FCSTD DOCUMENT  (FreeCAD 1.1R38827 (Git))
Label: composit_stand3_tech_sector_assembly
License: All rights reserved
LicenseURL: http://en.wikipedia.org/wiki/All_rights_reserved
objects: App::Link×5, App::DocumentObjectGroup×3, PartDesign::CoordinateSystem×1, App::FeaturePython×1, App::Part×1
note: 1 computed .brp shape members not serialized (recipe doc carries the construction recipe); baked Part::Feature solids carry a one-line shape summary decoded from their .brp
EXTERNAL_REF file=composit_stand3_tech_sector_hor_model.FCStd obj=Local_CS
EXTERNAL_REF file=composit_stand3_tech_sector_hor_model.FCStd obj=Body
EXTERNAL_REF file=composit_stand3_tech_sector_hor_model.FCStd obj=Local_CS001
EXTERNAL_REF file=composit_stand3_tech_sector_pillar_model.FCStd obj=Local_CS
EXTERNAL_REF file=composit_stand3_tech_sector_pillar_model.FCStd obj=Body
EXTERNAL_REF file=composit_stand3_tech_sector_plexiglass_model.FCStd obj=Local_CS
EXTERNAL_REF file=composit_stand3_tech_sector_plexiglass_model.FCStd obj=Body
EXTERNAL_REF file=composit_stand3_tech_sector_pillar_model.FCStd obj=Local_CS001
EXTERNAL_REF file=composit_stand3_tech_sector_pillar_model.FCStd obj=Body002

FEATURE [App::DocumentObjectGroup] Parts
FEATURE [PartDesign::CoordinateSystem] LCS_Origin
  AttacherType = Attacher::AttachEngine3D
  AttachmentSupport = -> [X_Axis]
  MapMode = 2
FEATURE [App::DocumentObjectGroup] Constraints
FEATURE [App::FeaturePython] Variables  # WARN: FeaturePython — macro-defined, semantics opaque (R4)
  Type = App::PropertyContainer
FEATURE [App::DocumentObjectGroup] Configurations
FEATURE [App::Link] hor
  AttachedBy = #Local_CS
  AttachedTo = Parent Assembly#LCS_Origin
  LinkedObject = -> <external composit_stand3_tech_sector_hor_model.FCStd>#Body
  SolverId = Asm4EE
  expr: Placement = LCS_Origin.Placement * AttachmentOffset * composit_stand3_tech_sector_hor_model#Local_CS.Placement ^ -1
FEATURE [App::Link] pillar
  AttachedBy = #Local_CS
  AttachedTo = hor#Local_CS001
  LinkPlacement = pos=(152.864,235.416,3) rot=(0,0,-1;0.523599rad)
  LinkedObject = -> <external composit_stand3_tech_sector_pillar_model.FCStd>#Body
  Placement = pos=(152.864,235.416,3) rot=(0,0,-1;0.523599rad)
  SolverId = Asm4EE
  expr: Placement = hor.Placement * composit_stand3_tech_sector_hor_model#Local_CS001.Placement * AttachmentOffset * composit_stand3_tech_sector_pillar_model#Local_CS.Placement ^ -1
FEATURE [App::Link] plexiglass
  AttachedBy = #Local_CS
  AttachedTo = Parent Assembly#LCS_Origin
  LinkedObject = -> <external composit_stand3_tech_sector_plexiglass_model.FCStd>#Body
  SolverId = Asm4EE
  expr: Placement = LCS_Origin.Placement * AttachmentOffset * composit_stand3_tech_sector_plexiglass_model#Local_CS.Placement ^ -1
FEATURE [App::Link] hor001
  AttachedBy = #Local_CS
  AttachedTo = Parent Assembly#LCS_Origin
  AttachmentOffset = pos=(0,0,419) rot=(1,0,0;3.14159rad)
  LinkPlacement = pos=(0,0,419) rot=(1,0,0;3.14159rad)
  LinkedObject = -> <external composit_stand3_tech_sector_hor_model.FCStd>#Body
  Placement = pos=(0,0,419) rot=(1,0,0;3.14159rad)
  SolverId = Asm4EE
  expr: Placement = LCS_Origin.Placement * AttachmentOffset * composit_stand3_tech_sector_hor_model#Local_CS.Placement ^ -1
FEATURE [App::Link] pillar_mirror
  AttachedBy = #Local_CS001
  AttachedTo = hor001#Local_CS001
  LinkPlacement = pos=(152.864,-235.416,3) rot=(0.965926,0.258819,0;3.14159rad)
  LinkedObject = -> <external composit_stand3_tech_sector_pillar_model.FCStd>#Body002
  Placement = pos=(152.864,-235.416,3) rot=(0.965926,0.258819,0;3.14159rad)
  SolverId = Asm4EE
  expr: Placement = hor001.Placement * composit_stand3_tech_sector_hor_model#Local_CS001.Placement * AttachmentOffset * composit_stand3_tech_sector_pillar_model#Local_CS001.Placement ^ -1
FEATURE [App::Part] Assembly
  AssemblyType = Part::Link
  Group = -> [LCS_Origin,Constraints,Variables,Configurations,hor,pillar,plexiglass,hor001,pillar_mirror]
  Origin = -> Origin
  Type = Assembly

RESOLVED EXTERNAL PARTS (link-assembly join: the EXTERNAL_REF files above that resolve inside this repo's crawl, each included once):
---- part composit_stand3_tech_sector_hor_model.FCStd = doc fcstd_c595c57b1264 ----
FCSTD DOCUMENT  (FreeCAD 1.1R38827 (Git))
Label: composit_stand3_tech_sector_hor_model
License: All rights reserved
LicenseURL: http://en.wikipedia.org/wiki/All_rights_reserved
objects: Part::FeaturePython×5, App::Link×3, PartDesign::SubShapeBinder×2, PartDesign::Body×2, PartDesign::CoordinateSystem×2, Part::Mirroring×1, PartDesign::Pad×1, Part::Cylinder×1, Part::MultiFuse×1, PartDesign::Boolean×1
note: 19 computed .brp shape members not serialized (recipe doc carries the construction recipe); baked Part::Feature solids carry a one-line shape summary decoded from their .brp
EXTERNAL_REF file=composit_stand3_tech_sector_hor_main.FCStd obj=Sketch
EXTERNAL_REF file=composit_stand3_tech_sector_plexiglass_main.FCStd obj=Placment
EXTERNAL_REF file=composit_stand3_tech_sector_hor_main.FCStd obj=Link001
EXTERNAL_REF file=composit_stand3_tech_sector_pillar_main.FCStd obj=ArrayFromShape

FEATURE [PartDesign::SubShapeBinder] Binder
  BindCopyOnChange = 0
  BindMode = 0
  ClaimChildren = true
  Fuse = false
  MakeFace = true
  OffsetFill = false
  OffsetIntersection = false
  OffsetJoinType = 0
  OffsetOpenResult = false
  PartialLoad = false
  Relative = true
  Support = -> [<external composit_stand3_tech_sector_hor_main.FCStd>#Sketch]
  _Version = 2
FEATURE [Part::Mirroring] Part__Mirroring  label="Binder (Mirror #1)"
  Base = (0,0,0)
  Normal = (0,1,0)
  Source = -> Binder
FEATURE [Part::FeaturePython] Connect  # WARN: FeaturePython — macro-defined, semantics opaque (R4)
  Objects = -> [Binder,Part__Mirroring]
  Tolerance = 0
FEATURE [PartDesign::SubShapeBinder] Binder001
  BindCopyOnChange = 0
  BindMode = 0
  ClaimChildren = true
  Context = -> Body [Binder001.]
  Fuse = false
  MakeFace = true
  OffsetFill = false
  OffsetIntersection = false
  OffsetJoinType = 0
  OffsetOpenResult = false
  PartialLoad = false
  Relative = false
  Support = -> [Connect]
  _Version = 2
FEATURE [PartDesign::Pad] Pad
  Direction = (0,0,1)
  Length = 3
  Length2 = 10
  Profile = -> Binder001
  Suppressed = false
  Type = 0
FEATURE [App::Link] Link001  label="edge_placement"
  LinkTransform = true
  LinkedObject = -> <external composit_stand3_tech_sector_plexiglass_main.FCStd>#Placment
FEATURE [App::Link] Link002  label="front_support_intersection_placement"
  LinkedObject = -> <external composit_stand3_tech_sector_hor_main.FCStd>#Link001
FEATURE [App::Link] Link003  label="holes_bottom"
  LinkedObject = -> <external composit_stand3_tech_sector_pillar_main.FCStd>#ArrayFromShape
FEATURE [Part::FeaturePython] Populate  label="Populate edge_placement with holes"  # WARN: FeaturePython — macro-defined, semantics opaque (R4)
  Copying = 0
  ExposePlacement = false
  MarkerShape = 1
  MarkerSize = 0
  NumElements = 3
  Object = -> Link003
  OutputCompounding = 0
  PlacementsFrom = -> Link002
  PlacementsTo = -> Link001
  Referencing = 3
  Type = lattice2PopulateCopies.LatticePopulateCopies
  isLattice = 1
FEATURE [Part::FeaturePython] Mirror  label="Mirror of Populate edge_placement with holes"  # WARN: FeaturePython — macro-defined, semantics opaque (R4)
  ExposePlacement = false
  FlipX = false
  FlipY = true
  FlipZ = false
  MarkerShape = 1
  MarkerSize = 0
  NumElements = 3
  Object = -> Populate
  ObjectTraversal = 0
  Type = lattice2Mirror.LatticeMirror
  isLattice = 1
FEATURE [Part::FeaturePython] Join  # WARN: FeaturePython — macro-defined, semantics opaque (R4)
  ExposePlacement = false
  Interleave = false
  Links = -> [Populate,Mirror]
  MarkerShape = 1
  MarkerSize = 0
  NumElements = 6
  Type = lattice2JoinArrays.JoinArrays
  isLattice = 1
FEATURE [Part::Cylinder] Cylinder  label="hole_3.4mm"
  Angle = 360
  AttacherType = Attacher::AttachEngine3D
  FirstAngle = 0
  Height = 10
  Radius = 2
  SecondAngle = 0
FEATURE [Part::FeaturePython] Populate001  label="Populate Join with hole_3.4mm"  # WARN: FeaturePython — macro-defined, semantics opaque (R4)
  Copying = 0
  ExposePlacement = false
  MarkerShape = 1
  MarkerSize = 0
  NumElements = 0
  Object = -> Cylinder
  OutputCompounding = 1
  PlacementsTo = -> Join
  Referencing = 0
  Type = lattice2PopulateCopies.LatticePopulateCopies
  isLattice = 0
FEATURE [PartDesign::Body] Body001
  AllowCompound = false
  Origin = -> Origin001
FEATURE [Part::MultiFuse] Fusion
  Shapes = -> [Populate001]
FEATURE [PartDesign::Boolean] Boolean
  BaseFeature = -> Pad
  Group = -> [Fusion]
  Suppressed = false
  Type = 1
  UsePlacement = true
FEATURE [PartDesign::CoordinateSystem] Local_CS  label="base_LCS"
  AttacherType = Attacher::AttachEngine3D
  AttachmentSupport = -> [XY_Plane]
  MapMode = 5
FEATURE [PartDesign::CoordinateSystem] Local_CS001  label="pillar_LCS"
  AttacherType = Attacher::AttachEngine3D
  AttachmentOffset = pos=(180.364,283.047,3) rot=(0,0,1;1.94804rad)
  AttachmentSupport = -> [XY_Plane]
  MapMode = 5
  Placement = pos=(180.364,283.047,3) rot=(0,0,1;1.94804rad)
  expr: AttachmentOffset = placement(vector(0; 0; 3); rotation(0; 0; 0)) * <<edge_placement>>.LinkedObject.Placement
FEATURE [PartDesign::Body] Body  label="hor"
  AllowCompound = false
  Group = -> [Binder001,Pad,Boolean,Local_CS,Local_CS001]
  Origin = -> Origin
  Tip = -> Boolean
---- part composit_stand3_tech_sector_pillar_model.FCStd = doc fcstd_bfc0236a88c2 ----
FCSTD DOCUMENT  (FreeCAD 1.1R38827 (Git))
Label: composit_stand3_tech_sector_pillar_model
License: All rights reserved
LicenseURL: http://en.wikipedia.org/wiki/All_rights_reserved
objects: PartDesign::Body×3, App::Link×3, PartDesign::SubShapeBinder×2, PartDesign::FeaturePython×2, PartDesign::CoordinateSystem×2, Part::FeaturePython×2, Part::Cylinder×1, Part::MultiFuse×1, PartDesign::Boolean×1, Part::Mirroring×1, PartDesign::FeatureBase×1
note: 20 computed .brp shape members not serialized (recipe doc carries the construction recipe); baked Part::Feature solids carry a one-line shape summary decoded from their .brp
EXTERNAL_REF file=composit_stand3_tech_sector_pillar_main.FCStd obj=Sketch
EXTERNAL_REF file=composit_stand3_tech_sector_main.FCStd obj=Spreadsheet
EXTERNAL_REF file=composit_stand3_tech_sector_pillar_main.FCStd obj=Placment
EXTERNAL_REF file=composit_stand3_tech_sector_pillar_main.FCStd obj=Join
EXTERNAL_REF file=composit_stand3_tech_sector_pillar_main.FCStd obj=Join001

FEATURE [PartDesign::SubShapeBinder] Binder
  BindCopyOnChange = 0
  BindMode = 0
  ClaimChildren = false
  Fuse = false
  MakeFace = true
  OffsetFill = false
  OffsetIntersection = false
  OffsetJoinType = 0
  OffsetOpenResult = false
  PartialLoad = false
  Relative = true
  Support = -> [<external composit_stand3_tech_sector_pillar_main.FCStd>#Sketch]
  _Version = 2
FEATURE [PartDesign::SubShapeBinder] Binder001
  BindCopyOnChange = 0
  BindMode = 0
  ClaimChildren = true
  Context = -> Body [Binder001.]
  Fuse = false
  MakeFace = true
  OffsetFill = false
  OffsetIntersection = false
  OffsetJoinType = 0
  OffsetOpenResult = false
  PartialLoad = false
  Placement = pos=(0,0,0.4) rot=(0,0,1;0rad)
  Relative = false
  Support = -> [Binder]
  _Version = 2
FEATURE [PartDesign::FeaturePython] BaseBend  # WARN: FeaturePython — macro-defined, semantics opaque (R4)
  BendSide = 0
  BendSketch = -> Binder001
  MidPlane = false
  Reverse = false
  Suppressed = false
  length = 412.2
  radius = 0.1
  thickness = 0.3
  expr: length = <<composit_stand3_tech_sector_main>>#<<Properties>>.height - 3 mm * 2 - 0.4 mm * 2
FEATURE [PartDesign::FeaturePython] Bend  # WARN: FeaturePython — macro-defined, semantics opaque (R4)
  AutoMiter = true
  BaseFeature = -> BaseBend
  BendType = 0
  LengthList = [15]
  LengthSpec = 0
  NonperforationMaxLength = 5
  Perforate = false
  PerforationAngle = 0
  PerforationInitialLength = 5
  PerforationMaxLength = 5
  ReliefFactor = 0.7
  Suppressed = false
  UseReliefFactor = false
  angle = 90
  baseObject = -> BaseBend [Edge11,Edge26,Edge42,Edge14,Edge29,Edge43]
  bendAList = [90]
  extend1 = 0
  extend2 = 0
  gap1 = 0
  gap2 = 0
  invert = false
  kfactor = 0.5
  length = 15
  maxExtendDist = 5
  minGap = 0.2
  minReliefGap = 1
  miterangle1 = 0
  miterangle2 = 0
  offset = 0
  radius = 0.1
  reliefType = 0
  reliefd = 1
  reliefw = 0.8
  sketchflip = false
  sketchinvert = false
  unfold = false
  expr: radius = BaseBend.radius
FEATURE [PartDesign::Body] Body001  label="Body"
  AllowCompound = false
  Origin = -> Origin001
FEATURE [App::Link] Link  label="front_support_intersection_placement"
  LinkTransform = true
  LinkedObject = -> <external composit_stand3_tech_sector_pillar_main.FCStd>#Placment
FEATURE [PartDesign::CoordinateSystem] Local_CS  label="edge_LCS"
  AttacherType = Attacher::AttachEngine3D
  AttachmentOffset = pos=(-3.6e-15,55,0) rot=(0,0,1;2.47164rad)
  AttachmentSupport = -> [XY_Plane]
  MapMode = 5
  Placement = pos=(-3.6e-15,55,0) rot=(0,0,1;2.47164rad)
  expr: AttachmentOffset = <<front_support_intersection_placement>>.LinkedObject.Placement
FEATURE [App::Link] Link001  label="holes"
  LinkedObject = -> <external composit_stand3_tech_sector_pillar_main.FCStd>#Join
FEATURE [Part::Cylinder] Cylinder
  Angle = 360
  AttacherType = Attacher::AttachEngine3D
  FirstAngle = 0
  Height = 9
  Radius = 1.7
  SecondAngle = 0
FEATURE [Part::FeaturePython] Populate  label="Populate holes with Cylinder"  # WARN: FeaturePython — macro-defined, semantics opaque (R4)
  Copying = 0
  ExposePlacement = false
  MarkerShape = 1
  MarkerSize = 0
  NumElements = 0
  Object = -> Cylinder
  OutputCompounding = 1
  PlacementsTo = -> Link001
  Referencing = 0
  Type = lattice2PopulateCopies.LatticePopulateCopies
  isLattice = 0
FEATURE [App::Link] Link002  label="plexiglass_fix_holes"
  LinkedObject = -> <external composit_stand3_tech_sector_pillar_main.FCStd>#Join001
FEATURE [Part::FeaturePython] Populate001  label="Populate plexiglass_fix_holes with Cylinder"  # WARN: FeaturePython — macro-defined, semantics opaque (R4)
  Copying = 0
  ExposePlacement = false
  MarkerShape = 1
  MarkerSize = 0
  NumElements = 0
  Object = -> Cylinder
  OutputCompounding = 1
  PlacementsTo = -> Link002
  Referencing = 0
  Type = lattice2PopulateCopies.LatticePopulateCopies
  isLattice = 0
FEATURE [Part::MultiFuse] Fusion
  Shapes = -> [Populate,Populate001]
FEATURE [PartDesign::Boolean] Boolean
  BaseFeature = -> Bend
  Group = -> [Fusion]
  Suppressed = false
  Type = 1
  UsePlacement = true
FEATURE [PartDesign::Body] Body  label="pillar"
  AllowCompound = false
  Group = -> [Binder001,BaseBend,Bend,Local_CS,Boolean]
  Origin = -> Origin
  Tip = -> Boolean
FEATURE [Part::Mirroring] Part__Mirroring  label="pillar (Mirror #1)"
  Base = (0,0,0)
  Normal = (0,0,1)
  Source = -> Body
FEATURE [PartDesign::FeatureBase] BaseFeature
  BaseFeature = -> Part__Mirroring
  Suppressed = false
FEATURE [PartDesign::CoordinateSystem] Local_CS001  label="mirror_LCS"
  AttacherType = Attacher::AttachEngine3D
  AttachmentOffset = pos=(-3.6e-15,55,-413) rot=(0,0,1;2.47164rad)
  AttachmentSupport = -> [XY_Plane002]
  MapMode = 5
  Placement = pos=(-3.6e-15,55,-413) rot=(0,0,1;2.47164rad)
  expr: AttachmentOffset = placement(vector(0; 0; -(<<composit_stand3_tech_sector_main>>#<<Properties>>.height - 6 mm)); rotation(0; 0; 0)) * <<front_support_intersection_placement>>.LinkedObject.Placement
FEATURE [PartDesign::Body] Body002  label="pillar_mirror"
  AllowCompound = false
  BaseFeature = -> Part__Mirroring
  Group = -> [BaseFeature,Local_CS001]
  Origin = -> Origin002
  Tip = -> BaseFeature
---- part composit_stand3_tech_sector_plexiglass_model.FCStd = doc fcstd_78f083bbaf73 ----
FCSTD DOCUMENT  (FreeCAD 1.1R38827 (Git))
Label: composit_stand3_tech_sector_plexiglass_model
License: All rights reserved
LicenseURL: http://en.wikipedia.org/wiki/All_rights_reserved
objects: Part::FeaturePython×20, App::Link×7, PartDesign::SubShapeBinder×2, Sketcher::SketchObject×2, PartDesign::Body×2, PartDesign::FeaturePython×1, PartDesign::CoordinateSystem×1, Part::Cylinder×1, Part::Extrusion×1, Part::MultiFuse×1, PartDesign::Boolean×1
note: 36 computed .brp shape members not serialized (recipe doc carries the construction recipe); baked Part::Feature solids carry a one-line shape summary decoded from their .brp
EXTERNAL_REF file=composit_stand3_tech_sector_plexiglass_main.FCStd obj=Sketch
EXTERNAL_REF file=composit_stand3_tech_sector_plexiglass_main.FCStd obj=Placment
EXTERNAL_REF file=composit_stand3_tech_sector_pillar_main.FCStd obj=Join001
EXTERNAL_REF file=composit_stand3_tech_sector_pillar_main.FCStd obj=Placment
EXTERNAL_REF file=composit_stand3_tech_sector_pillar_main.FCStd obj=LinearArray
EXTERNAL_REF file=composit_stand3_tech_sector_pillar_main.FCStd obj=Placment001
EXTERNAL_REF file=composit_stand3_tech_sector_plexiglass_main.FCStd obj=Placment001
EXTERNAL_REF file=../corner_small_14.5mm.FCStd obj=Binder001

FEATURE [PartDesign::SubShapeBinder] Binder
  BindCopyOnChange = 0
  BindMode = 0
  ClaimChildren = false
  Fuse = false
  MakeFace = true
  OffsetFill = false
  OffsetIntersection = false
  OffsetJoinType = 0
  OffsetOpenResult = false
  PartialLoad = false
  Relative = true
  Support = -> [<external composit_stand3_tech_sector_plexiglass_main.FCStd>#Sketch]
  _Version = 2
FEATURE [Sketcher::SketchObject] Sketch
  ArcFitTolerance = 0
  ExternalGeometry = -> [Binder]
  FullyConstrained = false
  MakeInternals = false
  sketch-geometry (4):
    g0: LineSegment StartX=180.364 StartY=283.047 StartZ=0 EndX=245 EndY=119.916 EndZ=0
    g1: LineSegment StartX=245 StartY=119.916 StartZ=0 EndX=245 EndY=-119.916 EndZ=0
    g2: LineSegment StartX=245 StartY=-119.916 StartZ=0 EndX=180.364 EndY=-283.047 EndZ=0
    g3: GeomPoint [constr] X=102.255 Y=14.9858 Z=0
  constraints (7):
    c: Coincident(g1,g2)
    c: Coincident(g0,g1)
    c: Symmetric(g2,g0,g-1)
    c: Symmetric(g0,g1,g-1)
    c: PointOnObject(g-3,g1)
    c: Coincident(g0,g-4)
    c: PointOnObject(g-4,g0)
FEATURE [PartDesign::SubShapeBinder] Binder001
  BindCopyOnChange = 0
  BindMode = 0
  ClaimChildren = false
  Context = -> Body [Binder001.]
  Fuse = false
  MakeFace = true
  OffsetFill = false
  OffsetIntersection = false
  OffsetJoinType = 0
  OffsetOpenResult = false
  PartialLoad = false
  Relative = true
  Support = -> [Sketch]
  _Version = 2
FEATURE [PartDesign::FeaturePython] BaseBend  # WARN: FeaturePython — macro-defined, semantics opaque (R4)
  BendSide = 1
  BendSketch = -> Binder001
  MidPlane = false
  Reverse = false
  Suppressed = false
  length = 419
  radius = 602
  thickness = 1
  expr: radius = composit_stand3_tech_sector_plexiglass_main#<<main_sketch>>.Constraints.r
FEATURE [PartDesign::CoordinateSystem] Local_CS  label="base_LCS"
  AttacherType = Attacher::AttachEngine3D
  AttachmentSupport = -> [XY_Plane]
  MapMode = 5
FEATURE [App::Link] Link  label="edge_placement"
  LinkClaimChild = true
  LinkTransform = true
  LinkedObject = -> <external composit_stand3_tech_sector_plexiglass_main.FCStd>#Placment
FEATURE [App::Link] Link001  label="plexiglass_fix_holes"
  LinkedObject = -> <external composit_stand3_tech_sector_pillar_main.FCStd>#Join001
FEATURE [App::Link] Link002  label="front_support_intersection_placement"
  LinkTransform = true
  LinkedObject = -> <external composit_stand3_tech_sector_pillar_main.FCStd>#Placment
FEATURE [Part::Cylinder] Cylinder  label="hole_3.4mm"
  Angle = 360
  AttacherType = Attacher::AttachEngine3D
  FirstAngle = 0
  Height = 10
  Placement = pos=(0,0,-5) rot=(0,0,1;0rad)
  Radius = 1.7
  SecondAngle = 0
FEATURE [PartDesign::Body] Body001  label="Body"
  AllowCompound = false
  Origin = -> Origin001
FEATURE [Part::FeaturePython] Placment  # WARN: FeaturePython — macro-defined, semantics opaque (R4)
  AttacherType = Attacher::AttachEngine3D
  ExposePlacement = true
  MarkerShape = 1
  MarkerSize = 50
  NumElements = 1
  Placement = pos=(0,0,3) rot=(0,0,1;0rad)
  Type = lattice2AttachablePlacement.AttachablePlacement
  isLattice = 1
FEATURE [Part::FeaturePython] Populate002  label="Populate edge_placement with Placment"  # WARN: FeaturePython — macro-defined, semantics opaque (R4)
  Copying = 0
  ExposePlacement = false
  MarkerShape = 1
  MarkerSize = 50
  NumElements = 1
  Object = -> Placment
  OutputCompounding = 0
  PlacementsTo = -> Link
  Referencing = 0
  Type = lattice2PopulateCopies.LatticePopulateCopies
  isLattice = 1
FEATURE [Part::FeaturePython] Populate  label="Populate edge_placement with plexiglass_fix_holes"  # WARN: FeaturePython — macro-defined, semantics opaque (R4)
  Copying = 0
  ExposePlacement = false
  MarkerShape = 1
  MarkerSize = 0
  NumElements = 2
  Object = -> Link001
  OutputCompounding = 0
  PlacementsFrom = -> Link002
  PlacementsTo = -> Populate002
  Referencing = 3
  Type = lattice2PopulateCopies.LatticePopulateCopies
  isLattice = 1
FEATURE [Part::FeaturePython] Mirror  label="Mirror of Populate edge_placement with plexiglass_fix_holes"  # WARN: FeaturePython — macro-defined, semantics opaque (R4)
  ExposePlacement = false
  FlipX = false
  FlipY = true
  FlipZ = false
  MarkerShape = 1
  MarkerSize = 0
  NumElements = 2
  Object = -> Populate
  ObjectTraversal = 0
  Type = lattice2Mirror.LatticeMirror
  isLattice = 1
FEATURE [Sketcher::SketchObject] Sketch001
  ArcFitTolerance = 0
  FullyConstrained = true
  MakeInternals = false
  Placement = pos=(0,0,0) rot=(0,0.707107,0.707107;3.14159rad)
  sketch-geometry (3):
    g0: ArcOfCircle CenterX=3 CenterY=3 CenterZ=0 NormalX=0 NormalY=0 NormalZ=1 AngleXU=0 Radius=3 StartAngle=3.14159 EndAngle=4.71239
    g1: LineSegment StartX=3 StartY=0 StartZ=0 EndX=0 EndY=0 EndZ=0
    g2: LineSegment StartX=0 StartY=0 StartZ=0 EndX=0 EndY=3 EndZ=0
  constraints (8):
    c: PointOnObject(g0,g-1)
    c: PointOnObject(g0,g-2)
    c: Coincident(g1,g2)
    c: Vertical(g2)
    c: Tangent(g0,g1) = 1.5708
    c: Tangent(g2,g0) = 1.5708
    c: Horizontal(g1)
    c: Radius(g0) = 3
FEATURE [Part::Extrusion] Extrude
  Base = -> Sketch001
  Dir = (0,1,-2e-16)
  DirMode = 2
  FaceMakerClass = Part::FaceMakerBullseye
  FaceMakerMode = 3
  LengthFwd = 10
  LengthRev = 0
  Solid = true
  Symmetric = true
FEATURE [Part::FeaturePython] Mirror001  label="Mirror001 of edge_placement"  # WARN: FeaturePython — macro-defined, semantics opaque (R4)
  ExposePlacement = false
  FlipX = false
  FlipY = false
  FlipZ = true
  MarkerShape = 1
  MarkerSize = 50
  NumElements = 1
  Object = -> Link
  ObjectTraversal = 0
  PivotPlacement = pos=(0,0,209.5) rot=(0,0,1;0rad)
  Type = lattice2Mirror.LatticeMirror
  isLattice = 1
  expr: .PivotPlacement.Base.z = <<BaseBend>>.length / 2
FEATURE [Part::FeaturePython] Join001  # WARN: FeaturePython — macro-defined, semantics opaque (R4)
  ExposePlacement = false
  Interleave = false
  Links = -> [Link,Mirror001]
  MarkerShape = 1
  MarkerSize = 0
  NumElements = 2
  Type = lattice2JoinArrays.JoinArrays
  isLattice = 1
FEATURE [Part::FeaturePython] Mirror002  label="Mirror002 of Join001"  # WARN: FeaturePython — macro-defined, semantics opaque (R4)
  ExposePlacement = false
  FlipX = false
  FlipY = true
  FlipZ = false
  MarkerShape = 1
  MarkerSize = 0
  NumElements = 2
  Object = -> Join001
  ObjectTraversal = 0
  Type = lattice2Mirror.LatticeMirror
  isLattice = 1
FEATURE [Part::FeaturePython] Join002  # WARN: FeaturePython — macro-defined, semantics opaque (R4)
  ExposePlacement = false
  Interleave = false
  Links = -> [Join001,Mirror002]
  MarkerShape = 1
  MarkerSize = 0
  NumElements = 4
  Type = lattice2JoinArrays.JoinArrays
  isLattice = 1
FEATURE [Part::FeaturePython] Populate003  label="Populate Join002 with Extrude"  # WARN: FeaturePython — macro-defined, semantics opaque (R4)
  Copying = 0
  ExposePlacement = false
  MarkerShape = 1
  MarkerSize = 0
  NumElements = 0
  Object = -> Extrude
  OutputCompounding = 1
  PlacementsTo = -> Join002
  Referencing = 0
  Type = lattice2PopulateCopies.LatticePopulateCopies
  isLattice = 0
FEATURE [App::Link] Link003  label="hand_holes_placement"
  LinkTransform = true
  LinkedObject = -> <external composit_stand3_tech_sector_pillar_main.FCStd>#LinearArray
FEATURE [App::Link] Link004  label="hand_placement"
  LinkTransform = true
  LinkedObject = -> <external composit_stand3_tech_sector_pillar_main.FCStd>#Placment001
FEATURE [Part::FeaturePython] Populate004  label="Populate Populate edge_placement with Placment with hand_placement"  # WARN: FeaturePython — macro-defined, semantics opaque (R4)
  Copying = 0
  ExposePlacement = false
  MarkerShape = 1
  MarkerSize = 20
  NumElements = 1
  Object = -> Link004
  OutputCompounding = 0
  PlacementsFrom = -> Link002
  PlacementsTo = -> Populate002
  Referencing = 3
  Type = lattice2PopulateCopies.LatticePopulateCopies
  isLattice = 1
FEATURE [Part::FeaturePython] Mirror003  label="Mirror003 of Populate Populate edge_placement with Placment with hand_placement"  # WARN: FeaturePython — macro-defined, semantics opaque (R4)
  ExposePlacement = false
  FlipX = false
  FlipY = true
  FlipZ = false
  MarkerShape = 1
  MarkerSize = 50
  NumElements = 1
  Object = -> Populate004
  ObjectTraversal = 0
  Type = lattice2Mirror.LatticeMirror
  isLattice = 1
FEATURE [Part::FeaturePython] Join003  # WARN: FeaturePython — macro-defined, semantics opaque (R4)
  ExposePlacement = false
  Interleave = false
  Links = -> [Populate004,Mirror003]
  MarkerShape = 1
  MarkerSize = 0
  NumElements = 2
  Type = lattice2JoinArrays.JoinArrays
  isLattice = 1
FEATURE [Part::FeaturePython] Populate005  label="Populate Join003 with hand_holes_placement"  # WARN: FeaturePython — macro-defined, semantics opaque (R4)
  Copying = 0
  ExposePlacement = false
  MarkerShape = 1
  MarkerSize = 0
  NumElements = 4
  Object = -> Link003
  OutputCompounding = 0
  PlacementsTo = -> Join003
  Referencing = 0
  Type = lattice2PopulateCopies.LatticePopulateCopies
  isLattice = 1
FEATURE [App::Link] Link005  label="fix_corner_placement"
  LinkTransform = true
  LinkedObject = -> <external composit_stand3_tech_sector_plexiglass_main.FCStd>#Placment001
FEATURE [App::Link] Link006  label="vert_hole"
  LinkedObject = -> <external ../corner_small_14.5mm.FCStd>#Binder001
FEATURE [Part::FeaturePython] Downgrade  label="Wires of vert_hole"  # WARN: FeaturePython — macro-defined, semantics opaque (R4)
  Base = -> Link006
  Mode = 7
FEATURE [Part::FeaturePython] ArrayFromShape  label="Array from Wires of vert_hole"  # WARN: FeaturePython — macro-defined, semantics opaque (R4)
  CompoundTraversal = 1
  ExposePlacement = false
  MarkerShape = 1
  MarkerSize = 5
  NumElements = 1
  OrientElementIndex = 0
  OrientMode = 4
  Placement = pos=(0,0,0) rot=(0,0,1;1.55334rad)
  ShapeLink = -> Downgrade
  TranslateElementIndex = 0
  TranslateMode = 3
  Type = lattice2ArrayFromShape.LatticeArrayFromShape
  isLattice = 1
FEATURE [Part::FeaturePython] Populate006  label="Populate fix_corner_placement with Array from Wires of vert_hole"  # WARN: FeaturePython — macro-defined, semantics opaque (R4)
  Copying = 0
  ExposePlacement = false
  MarkerShape = 1
  MarkerSize = 50
  NumElements = 1
  Object = -> ArrayFromShape
  OutputCompounding = 0
  PlacementsTo = -> Link005
  Referencing = 0
  Type = lattice2PopulateCopies.LatticePopulateCopies
  isLattice = 1
FEATURE [Part::FeaturePython] Mirror004  label="Mirror004 of Populate fix_corner_placement with Array from Wires of vert_hole"  # WARN: FeaturePython — macro-defined, semantics opaque (R4)
  ExposePlacement = false
  FlipX = false
  FlipY = false
  FlipZ = true
  MarkerShape = 1
  MarkerSize = 50
  NumElements = 1
  Object = -> Populate006
  ObjectTraversal = 0
  PivotPlacement = pos=(0,0,209.5) rot=(0,0,1;0rad)
  Type = lattice2Mirror.LatticeMirror
  isLattice = 1
  expr: .PivotPlacement.Base.z = <<BaseBend>>.length / 2
FEATURE [Part::FeaturePython] Join004  # WARN: FeaturePython — macro-defined, semantics opaque (R4)
  ExposePlacement = false
  Interleave = false
  Links = -> [Populate006,Mirror004]
  MarkerShape = 1
  MarkerSize = 0
  NumElements = 2
  Type = lattice2JoinArrays.JoinArrays
  isLattice = 1
FEATURE [Part::FeaturePython] Join  # WARN: FeaturePython — macro-defined, semantics opaque (R4)
  ExposePlacement = false
  Interleave = false
  Links = -> [Populate,Mirror,Populate005,Join004]
  MarkerShape = 1
  MarkerSize = 0
  NumElements = 10
  Type = lattice2JoinArrays.JoinArrays
  isLattice = 1
FEATURE [Part::FeaturePython] Populate001  label="Populate Join with hole_3.4mm"  # WARN: FeaturePython — macro-defined, semantics opaque (R4)
  Copying = 0
  ExposePlacement = false
  MarkerShape = 1
  MarkerSize = 0
  NumElements = 0
  Object = -> Cylinder
  OutputCompounding = 1
  PlacementsTo = -> Join
  Referencing = 0
  Type = lattice2PopulateCopies.LatticePopulateCopies
  isLattice = 0
FEATURE [Part::MultiFuse] Fusion
  Shapes = -> [Populate001,Populate003]
FEATURE [PartDesign::Boolean] Boolean
  BaseFeature = -> BaseBend
  Group = -> [Fusion]
  Suppressed = false
  Type = 1
  UsePlacement = true
FEATURE [PartDesign::Body] Body  label="plexiglass"
  AllowCompound = false
  Group = -> [Binder001,BaseBend,Local_CS,Boolean]
  Origin = -> Origin
  Tip = -> Boolean
